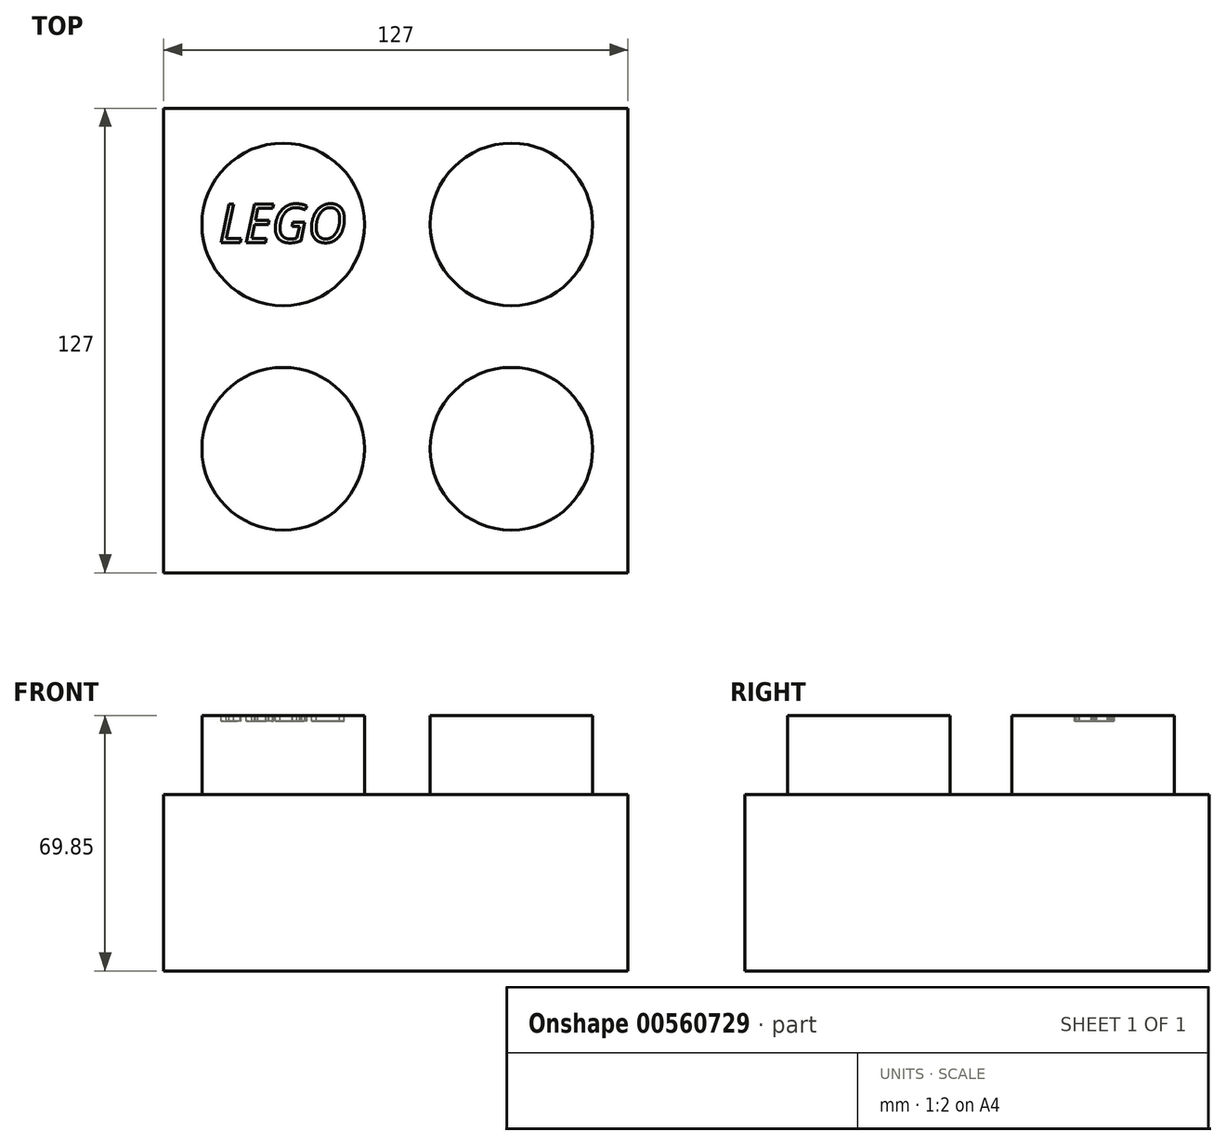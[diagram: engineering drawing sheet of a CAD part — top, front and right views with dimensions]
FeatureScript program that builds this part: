
annotation { "Feature Type Name" : "Feature", "Feature Type Description" : "" }
export const myFeature = defineFeature(function(context is Context, id is Id, definition is map)
    precondition{}
    {
        {
            var Q0;
            Q0=qCreatedBy(makeId("Top.planeOp"),FACE);
            var sketch = newSketch(context, id + "F0", { "sketchPlane" : qUnion([Q0])});
            skLineSegment(sketch, "E0.bottom", {"start": v(63.5, -63.5) * mm, "end": v(-63.5, -63.5) * mm});
            skLineSegment(sketch, "E0.top", {"start": v(63.5, 63.5) * mm, "end": v(-63.5, 63.5) * mm});
            skLineSegment(sketch, "E0.left", {"start": v(63.5, -63.5) * mm, "end": v(63.5, 63.5) * mm});
            skLineSegment(sketch, "E0.right", {"start": v(-63.5, -63.5) * mm, "end": v(-63.5, 63.5) * mm});
            skPoint(sketch, "E0.middle", {"position": v(0, 0) * mm});
            skSolve(sketch);
        }
        {
            var Q0;
            Q0=makeQuery(id+"F0.imprint","IMPRINT",FACE,{"disambiguationData":[TD([[makeQuery(id+"F0.imprint","IMPRINT",EDGE,{"derivedFrom":sQuery(id+"F0.wireOp",EDGE,"E0.bottom")}),-1.0]])]});
            extrude(context, id + "F1", {"entities" : qUnion([Q0]), "depth" : 48.26 * mm, "offsetDistance" : 25.4 * mm});
        }
        {
            var Q0;
            Q0=makeQuery(id+"F1.opExtrude","CAP_FACE",FACE,{"disambiguationData":[OSD([sQuery(id+"F0.wireOp",EDGE,"E0.bottom"),sQuery(id+"F0.wireOp",EDGE,"E0.top"),sQuery(id+"F0.wireOp",EDGE,"E0.left"),sQuery(id+"F0.wireOp",EDGE,"E0.right")])],"isStart":false});
            var sketch = newSketch(context, id + "F2", { "sketchPlane" : qUnion([Q0])});
            skCircle(sketch, "E1", {"center": v(-30.82, 31.73) * mm, "radius": 22.23 * mm});
            skCircle(sketch, "E2", {"center": v(31.63, 31.73) * mm, "radius": 22.23 * mm});
            skCircle(sketch, "E3", {"center": v(-30.82, -29.6) * mm, "radius": 22.23 * mm});
            skCircle(sketch, "E4", {"center": v(31.63, -29.6) * mm, "radius": 22.23 * mm});
            skSolve(sketch);
        }
        {
            var Q0;
            Q0=makeQuery(id+"F2.imprint","IMPRINT",FACE,{"disambiguationData":[TD([[makeQuery(id+"F2.imprint","IMPRINT",EDGE,{"derivedFrom":sQuery(id+"F2.wireOp",EDGE,"E1")}),1.0]])]});
            var Q1;
            Q1=makeQuery(id+"F2.imprint","IMPRINT",FACE,{"disambiguationData":[TD([[makeQuery(id+"F2.imprint","IMPRINT",EDGE,{"derivedFrom":sQuery(id+"F2.wireOp",EDGE,"E2")}),1.0]])]});
            var Q2;
            Q2=makeQuery(id+"F2.imprint","IMPRINT",FACE,{"disambiguationData":[TD([[makeQuery(id+"F2.imprint","IMPRINT",EDGE,{"derivedFrom":sQuery(id+"F2.wireOp",EDGE,"E4")}),1.0]])]});
            var Q3;
            Q3=makeQuery(id+"F2.imprint","IMPRINT",FACE,{"disambiguationData":[TD([[makeQuery(id+"F2.imprint","IMPRINT",EDGE,{"derivedFrom":sQuery(id+"F2.wireOp",EDGE,"E3")}),1.0]])]});
            extrude(context, id + "F3", {"entities" : qUnion([Q0, Q1, Q2, Q3]), "operationType" : NewBodyOperationType.ADD, "depth" : 21.59 * mm, "offsetDistance" : 25.4 * mm});
        }
        {
            var Q0;
            Q0=makeQuery(id+"F3.opExtrude","CAP_FACE",FACE,{"disambiguationData":[OSD([sQuery(id+"F2.wireOp",EDGE,"E1")])],"isStart":false});
            var sketch = newSketch(context, id + "F4", { "sketchPlane" : qUnion([Q0])});
            skText(sketch, "E5", { "text": "LEGO", "fontName": "OpenSans-Italic.ttf"});
            const initialGuessF4  = {"E5": [-0.04845, 0.0268, 1, 0, 0.01053]};
            skSetInitialGuess(sketch, initialGuessF4);
            skSolve(sketch);
        }
        {
            var Q0;
            Q0 = qSketchRegion(id + "F4", true);
            extrude(context, id + "F5", {"entities" : qUnion([Q0]), "operationType" : NewBodyOperationType.REMOVE, "oppositeDirection" : true, "depth" : 1.52 * mm, "offsetDistance" : 25.4 * mm});
        }
    });
